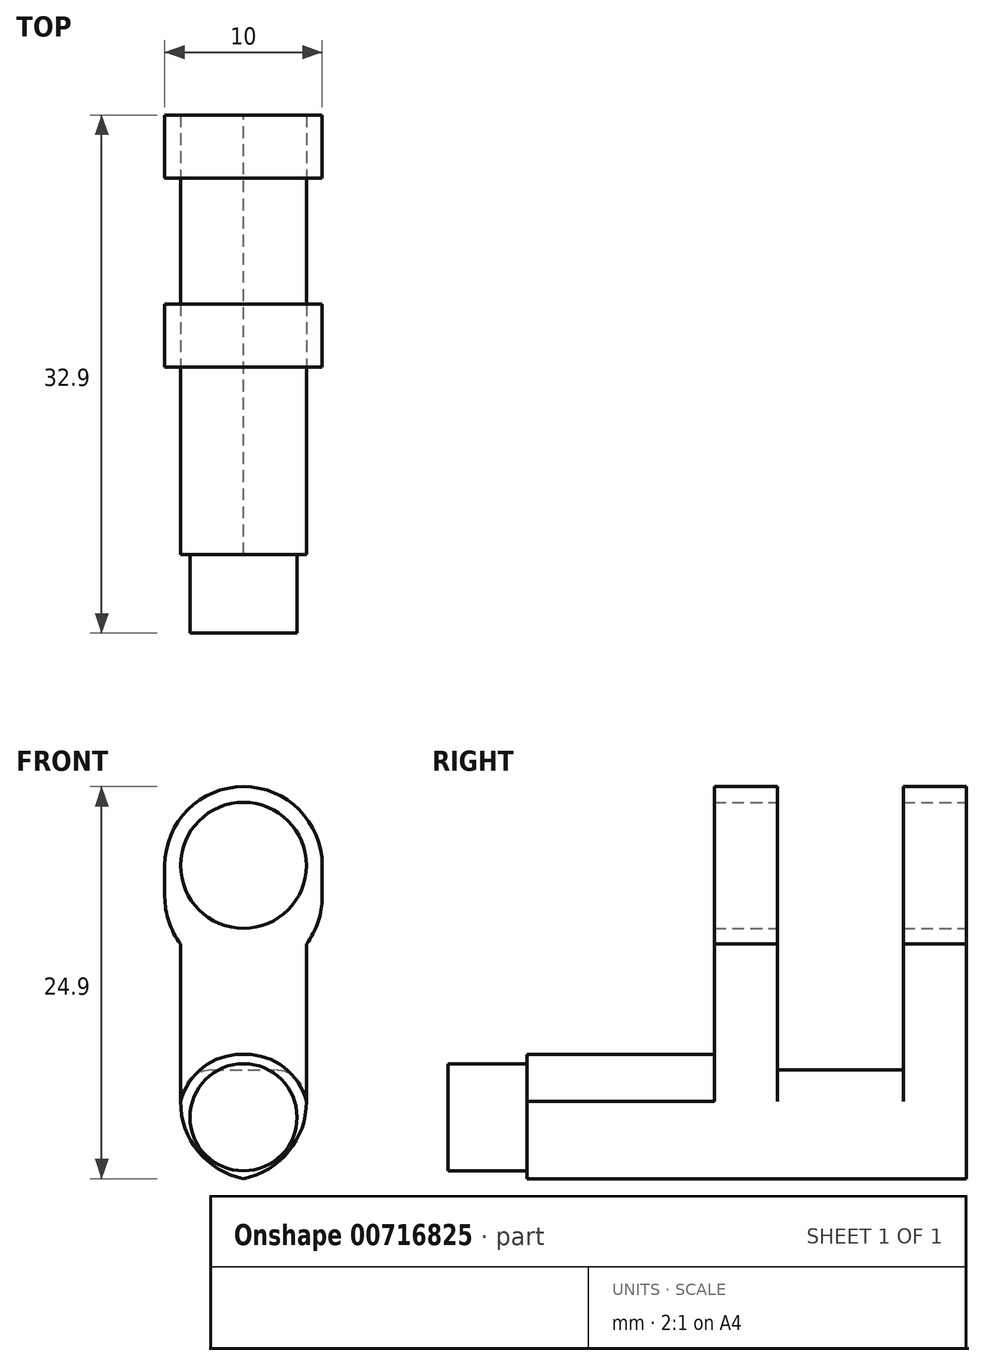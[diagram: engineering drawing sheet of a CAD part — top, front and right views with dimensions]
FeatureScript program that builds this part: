
annotation { "Feature Type Name" : "Feature", "Feature Type Description" : "" }
export const myFeature = defineFeature(function(context is Context, id is Id, definition is map)
    precondition{}
    {
        {
            var Q0;
            Q0=qCreatedBy(makeId("Front.planeOp"),FACE);
            var sketch = newSketch(context, id + "F0", { "sketchPlane" : qUnion([Q0])});
            skCircle(sketch, "E0", {"center": v(0, 0) * mm, "radius": 3.4 * mm});
            skSolve(sketch);
        }
        {
            var Q0;
            Q0=makeQuery(id+"F0.imprint","IMPRINT",FACE,{"disambiguationData":[TD([[makeQuery(id+"F0.imprint","IMPRINT",EDGE,{"derivedFrom":sQuery(id+"F0.wireOp",EDGE,"E0")}),1.0]])]});
            extrude(context, id + "F1", {"entities" : qUnion([Q0]), "depth" : 5 * mm, "offsetDistance" : 25 * mm});
        }
        {
            var Q0;
            Q0=makeQuery(id+"F1.opExtrude","CAP_FACE",FACE,{"disambiguationData":[OSD([sQuery(id+"F0.wireOp",EDGE,"E0")])],"isStart":true});
            var sketch = newSketch(context, id + "F2", { "sketchPlane" : qUnion([Q0])});
            skLineSegment(sketch, "E1.bottom", {"start": v(4, 4) * mm, "end": v(-4, 4) * mm});
            skLineSegment(sketch, "E1.top", {"start": v(4, -4) * mm, "end": v(-4, -4) * mm});
            skLineSegment(sketch, "E1.left", {"start": v(4, 4) * mm, "end": v(4, -4) * mm});
            skLineSegment(sketch, "E1.right", {"start": v(-4, 4) * mm, "end": v(-4, -4) * mm});
            skPoint(sketch, "E1.middle", {"position": v(0, 0) * mm});
            skSolve(sketch);
        }
        {
            var Q0;
            Q0 = qSketchRegion(id + "F2", true);
            extrude(context, id + "F3", {"entities" : qUnion([Q0]), "operationType" : NewBodyOperationType.ADD, "depth" : 14.9 * mm, "offsetDistance" : 25 * mm});
        }
        {
            var Q0;
            Q0=makeQuery(id+"F3.opExtrude","CAP_FACE",FACE,{"disambiguationData":[OSD([sQuery(id+"F2.wireOp",EDGE,"E1.bottom"),sQuery(id+"F2.wireOp",EDGE,"E1.top"),sQuery(id+"F2.wireOp",EDGE,"E1.left"),sQuery(id+"F2.wireOp",EDGE,"E1.right")])],"isStart":false});
            var sketch = newSketch(context, id + "F4", { "sketchPlane" : qUnion([Q0])});
            skLineSegment(sketch, "E2.bottom", {"start": v(-4, -4) * mm, "end": v(4, -4) * mm});
            skLineSegment(sketch, "E2.top", {"start": v(-4, 21) * mm, "end": v(4, 21) * mm});
            skLineSegment(sketch, "E2.left", {"start": v(-4, -4) * mm, "end": v(-4, 21) * mm});
            skLineSegment(sketch, "E2.right", {"start": v(4, -4) * mm, "end": v(4, 21) * mm});
            skSolve(sketch);
        }
        {
            var Q0;
            Q0 = qSketchRegion(id + "F4", true);
            extrude(context, id + "F5", {"entities" : qUnion([Q0]), "operationType" : NewBodyOperationType.ADD, "depth" : 10 * mm, "offsetDistance" : 25 * mm});
        }
        {
            var Q0;
            Q0=makeQuery(id+"F5.opExtrude","CAP_FACE",FACE,{"disambiguationData":[OSD([sQuery(id+"F4.wireOp",EDGE,"E2.bottom"),sQuery(id+"F4.wireOp",EDGE,"E2.top"),sQuery(id+"F4.wireOp",EDGE,"E2.left"),sQuery(id+"F4.wireOp",EDGE,"E2.right")])],"isStart":false});
            var sketch = newSketch(context, id + "F6", { "sketchPlane" : qUnion([Q0])});
            skLineSegment(sketch, "E3.bottom", {"start": v(-5, 21) * mm, "end": v(5, 21) * mm});
            skLineSegment(sketch, "E3.top", {"start": v(-5, 11) * mm, "end": v(5, 11) * mm});
            skLineSegment(sketch, "E3.left", {"start": v(-5, 21) * mm, "end": v(-5, 11) * mm});
            skLineSegment(sketch, "E3.right", {"start": v(5, 21) * mm, "end": v(5, 11) * mm});
            skSolve(sketch);
        }
        {
            var Q0;
            Q0 = qSketchRegion(id + "F6", true);
            extrude(context, id + "F7", {"entities" : qUnion([Q0]), "operationType" : NewBodyOperationType.ADD, "oppositeDirection" : true, "depth" : 10 * mm, "offsetDistance" : 25 * mm});
        }
        {
            var Q0;
            Q0=makeQuery(id+"F7.boolean.opBoolean","MERGE",FACE,{"derivedFrom":[makeQuery(id+"F5.opExtrude","CAP_FACE",FACE,{"disambiguationData":[OSD([sQuery(id+"F4.wireOp",EDGE,"E2.bottom"),sQuery(id+"F4.wireOp",EDGE,"E2.top"),sQuery(id+"F4.wireOp",EDGE,"E2.left"),sQuery(id+"F4.wireOp",EDGE,"E2.right")])],"isStart":false}),makeQuery(id+"F7.opExtrude","CAP_FACE",FACE,{"disambiguationData":[OSD([sQuery(id+"F6.wireOp",EDGE,"E3.bottom"),sQuery(id+"F6.wireOp",EDGE,"E3.top"),sQuery(id+"F6.wireOp",EDGE,"E3.left"),sQuery(id+"F6.wireOp",EDGE,"E3.right")])],"isStart":true})]});
            var sketch = newSketch(context, id + "F8", { "sketchPlane" : qUnion([Q0])});
            skCircle(sketch, "E4", {"center": v(0, 16) * mm, "radius": 4 * mm});
            skSolve(sketch);
        }
        {
            var Q0;
            Q0 = qSketchRegion(id + "F8", true);
            extrude(context, id + "F9", {"entities" : qUnion([Q0]), "operationType" : NewBodyOperationType.REMOVE, "endBound" : BoundingType.UP_TO_NEXT, "oppositeDirection" : true, "depth" : 25 * mm, "offsetDistance" : 25 * mm});
        }
        {
            var Q0;
            Q0=makeQuery(id+"F7.boolean.opBoolean","MERGE",FACE,{"derivedFrom":[makeQuery(id+"F5.opExtrude","SWEPT_FACE",FACE,{"disambiguationData":[OSD([sQuery(id+"F4.wireOp",EDGE,"E2.top")])]}),makeQuery(id+"F7.opExtrude","SWEPT_FACE",FACE,{"disambiguationData":[OSD([sQuery(id+"F6.wireOp",EDGE,"E3.bottom")])]})]});
            var sketch = newSketch(context, id + "F10", { "sketchPlane" : qUnion([Q0])});
            skLineSegment(sketch, "E5.bottom", {"start": v(-5, 23.9) * mm, "end": v(5, 23.9) * mm});
            skLineSegment(sketch, "E5.top", {"start": v(-5, 15.9) * mm, "end": v(5, 15.9) * mm});
            skLineSegment(sketch, "E5.left", {"start": v(-5, 23.9) * mm, "end": v(-5, 15.9) * mm});
            skLineSegment(sketch, "E5.right", {"start": v(5, 23.9) * mm, "end": v(5, 15.9) * mm});
            skSolve(sketch);
        }
        {
            var Q0;
            Q0 = qSketchRegion(id + "F10", true);
            extrude(context, id + "F11", {"entities" : qUnion([Q0]), "operationType" : NewBodyOperationType.REMOVE, "oppositeDirection" : true, "depth" : 18 * mm, "offsetDistance" : 25 * mm});
        }
        {
            var Q0;
            {var subQ0=sQuery(id+"F6.wireOp",EDGE,"E3.left");var subQ1=sQuery(id+"F6.wireOp",EDGE,"E3.top");Q0=makeQuery(id+"F11.boolean.opBoolean","SPLIT",EDGE,{"disambiguationData":[TD([makeQuery(id+"F11.opExtrude","SWEPT_FACE",FACE,{"disambiguationData":[OSD([sQuery(id+"F10.wireOp",EDGE,"E5.top")])]})])],"derivedFrom":makeQuery(id+"F7.opExtrude","SWEPT_EDGE",EDGE,{"disambiguationData":[OSD([subQ1,subQ0])]})});}
            var Q1;
            {var subQ0=sQuery(id+"F6.wireOp",EDGE,"E3.left");var subQ1=sQuery(id+"F6.wireOp",EDGE,"E3.top");Q1=makeQuery(id+"F11.boolean.opBoolean","SPLIT",EDGE,{"disambiguationData":[TD([makeQuery(id+"F11.opExtrude","SWEPT_FACE",FACE,{"disambiguationData":[OSD([sQuery(id+"F10.wireOp",EDGE,"E5.bottom")])]})])],"derivedFrom":makeQuery(id+"F7.opExtrude","SWEPT_EDGE",EDGE,{"disambiguationData":[OSD([subQ1,subQ0])]})});}
            var Q2;
            {var subQ0=sQuery(id+"F6.wireOp",EDGE,"E3.right");var subQ1=sQuery(id+"F6.wireOp",EDGE,"E3.top");Q2=makeQuery(id+"F11.boolean.opBoolean","SPLIT",EDGE,{"disambiguationData":[TD([makeQuery(id+"F11.opExtrude","SWEPT_FACE",FACE,{"disambiguationData":[OSD([sQuery(id+"F10.wireOp",EDGE,"E5.top")])]})])],"derivedFrom":makeQuery(id+"F7.opExtrude","SWEPT_EDGE",EDGE,{"disambiguationData":[OSD([subQ1,subQ0])]})});}
            var Q3;
            {var subQ0=sQuery(id+"F6.wireOp",EDGE,"E3.right");var subQ1=sQuery(id+"F6.wireOp",EDGE,"E3.top");Q3=makeQuery(id+"F11.boolean.opBoolean","SPLIT",EDGE,{"disambiguationData":[TD([makeQuery(id+"F11.opExtrude","SWEPT_FACE",FACE,{"disambiguationData":[OSD([sQuery(id+"F10.wireOp",EDGE,"E5.bottom")])]})])],"derivedFrom":makeQuery(id+"F7.opExtrude","SWEPT_EDGE",EDGE,{"disambiguationData":[OSD([subQ1,subQ0])]})});}
            var Q4;
            {var subQ0=sQuery(id+"F6.wireOp",EDGE,"E3.right");var subQ1=sQuery(id+"F6.wireOp",EDGE,"E3.bottom");Q4=makeQuery(id+"F11.boolean.opBoolean","SPLIT",EDGE,{"disambiguationData":[TD([makeQuery(id+"F11.opExtrude","SWEPT_FACE",FACE,{"disambiguationData":[OSD([sQuery(id+"F10.wireOp",EDGE,"E5.bottom")])]})])],"derivedFrom":makeQuery(id+"F7.opExtrude","SWEPT_EDGE",EDGE,{"disambiguationData":[OSD([subQ1,subQ0])]})});}
            var Q5;
            {var subQ0=sQuery(id+"F6.wireOp",EDGE,"E3.left");var subQ1=sQuery(id+"F6.wireOp",EDGE,"E3.bottom");Q5=makeQuery(id+"F11.boolean.opBoolean","SPLIT",EDGE,{"disambiguationData":[TD([makeQuery(id+"F11.opExtrude","SWEPT_FACE",FACE,{"disambiguationData":[OSD([sQuery(id+"F10.wireOp",EDGE,"E5.bottom")])]})])],"derivedFrom":makeQuery(id+"F7.opExtrude","SWEPT_EDGE",EDGE,{"disambiguationData":[OSD([subQ1,subQ0])]})});}
            var Q6;
            {var subQ0=sQuery(id+"F6.wireOp",EDGE,"E3.bottom");var subQ2=sQuery(id+"F6.wireOp",EDGE,"E3.right");Q6=makeQuery(id+"F11.boolean.opBoolean","SPLIT",EDGE,{"disambiguationData":[TD([makeQuery(id+"F11.opExtrude","SWEPT_FACE",FACE,{"disambiguationData":[OSD([sQuery(id+"F10.wireOp",EDGE,"E5.top")])]})])],"derivedFrom":makeQuery(id+"F7.opExtrude","SWEPT_EDGE",EDGE,{"disambiguationData":[OSD([subQ0,subQ2])]})});}
            var Q7;
            {var subQ0=sQuery(id+"F6.wireOp",EDGE,"E3.bottom");var subQ2=sQuery(id+"F6.wireOp",EDGE,"E3.left");Q7=makeQuery(id+"F11.boolean.opBoolean","SPLIT",EDGE,{"disambiguationData":[TD([makeQuery(id+"F11.opExtrude","SWEPT_FACE",FACE,{"disambiguationData":[OSD([sQuery(id+"F10.wireOp",EDGE,"E5.top")])]})])],"derivedFrom":makeQuery(id+"F7.opExtrude","SWEPT_EDGE",EDGE,{"disambiguationData":[OSD([subQ0,subQ2])]})});}
            fillet(context, id + "F12", {"entities" : qUnion([Q0, Q1, Q2, Q3, Q4, Q5, Q6, Q7]), "radius" : 5 * mm, "tangentPropagation" : true, "allowEdgeOverflow" : false});
        }
        {
            var Q0;
            Q0=makeQuery(id+"F7.boolean.opBoolean","MERGE",FACE,{"derivedFrom":[makeQuery(id+"F5.opExtrude","CAP_FACE",FACE,{"disambiguationData":[OSD([sQuery(id+"F4.wireOp",EDGE,"E2.bottom"),sQuery(id+"F4.wireOp",EDGE,"E2.top"),sQuery(id+"F4.wireOp",EDGE,"E2.left"),sQuery(id+"F4.wireOp",EDGE,"E2.right")])],"isStart":false}),makeQuery(id+"F7.opExtrude","CAP_FACE",FACE,{"disambiguationData":[OSD([sQuery(id+"F6.wireOp",EDGE,"E3.bottom"),sQuery(id+"F6.wireOp",EDGE,"E3.top"),sQuery(id+"F6.wireOp",EDGE,"E3.left"),sQuery(id+"F6.wireOp",EDGE,"E3.right")])],"isStart":true})]});
            var sketch = newSketch(context, id + "F13", { "sketchPlane" : qUnion([Q0])});
            skArc(sketch, "E6.0.0", {"start": v(5, 16) * mm, "mid": v(0, 21) * mm, "end": v(-5, 16) * mm});
            skLineSegment(sketch, "E6.0.1", {"start": v(-5, 16) * mm, "end": v(-5, 14) * mm});
            skArc(sketch, "E6.0.2", {"start": v(-5, 14) * mm, "mid": v(-4.74, 12.42) * mm, "end": v(-4, 11) * mm});
            skLineSegment(sketch, "E6.0.3", {"start": v(-4, 11) * mm, "end": v(-4, -4) * mm});
            skLineSegment(sketch, "E6.0.4", {"start": v(-4, -4) * mm, "end": v(4, -4) * mm});
            skLineSegment(sketch, "E6.0.5", {"start": v(4, -4) * mm, "end": v(4, 11) * mm});
            skArc(sketch, "E6.0.6", {"start": v(4, 11) * mm, "mid": v(4.74, 12.42) * mm, "end": v(5, 14) * mm});
            skLineSegment(sketch, "E6.0.7", {"start": v(5, 14) * mm, "end": v(5, 16) * mm});
            skCircle(sketch, "E7.0", {"center": v(0, 16) * mm, "radius": 4 * mm});
            skSolve(sketch);
        }
        {
            var Q0;
            Q0 = qSketchRegion(id + "F13", true);
            extrude(context, id + "F14", {"entities" : qUnion([Q0]), "operationType" : NewBodyOperationType.ADD, "depth" : 3 * mm, "offsetDistance" : 25 * mm});
        }
        {
            var Q0;
            Q0=makeQuery(id+"F7.boolean.opBoolean","MERGE",FACE,{"derivedFrom":[makeQuery(id+"F5.opExtrude","CAP_FACE",FACE,{"disambiguationData":[OSD([sQuery(id+"F4.wireOp",EDGE,"E2.bottom"),sQuery(id+"F4.wireOp",EDGE,"E2.top"),sQuery(id+"F4.wireOp",EDGE,"E2.left"),sQuery(id+"F4.wireOp",EDGE,"E2.right")])],"isStart":true}),makeQuery(id+"F7.opExtrude","CAP_FACE",FACE,{"disambiguationData":[OSD([sQuery(id+"F6.wireOp",EDGE,"E3.bottom"),sQuery(id+"F6.wireOp",EDGE,"E3.top"),sQuery(id+"F6.wireOp",EDGE,"E3.left"),sQuery(id+"F6.wireOp",EDGE,"E3.right")])],"isStart":false})]});
            var sketch = newSketch(context, id + "F15", { "sketchPlane" : qUnion([Q0])});
            skLineSegment(sketch, "E8.0.0", {"start": v(4, 4) * mm, "end": v(4, 11) * mm});
            skArc(sketch, "E8.0.1", {"start": v(4, 11) * mm, "mid": v(4.74, 12.42) * mm, "end": v(5, 14) * mm});
            skLineSegment(sketch, "E8.0.2", {"start": v(5, 14) * mm, "end": v(5, 16) * mm});
            skArc(sketch, "E8.0.3", {"start": v(5, 16) * mm, "mid": v(0, 21) * mm, "end": v(-5, 16) * mm});
            skLineSegment(sketch, "E8.0.4", {"start": v(-5, 16) * mm, "end": v(-5, 14) * mm});
            skArc(sketch, "E8.0.5", {"start": v(-5, 14) * mm, "mid": v(-4.74, 12.42) * mm, "end": v(-4, 11) * mm});
            skLineSegment(sketch, "E8.0.6", {"start": v(-4, 11) * mm, "end": v(-4, 4) * mm});
            skLineSegment(sketch, "E8.0.7", {"start": v(-4, 4) * mm, "end": v(4, 4) * mm});
            skCircle(sketch, "E9.0", {"center": v(0, 16) * mm, "radius": 4 * mm});
            skSolve(sketch);
        }
        {
            var Q0;
            Q0 = qSketchRegion(id + "F15", true);
            extrude(context, id + "F16", {"entities" : qUnion([Q0]), "operationType" : NewBodyOperationType.ADD, "depth" : 3 * mm, "offsetDistance" : 25 * mm});
        }
        {
            var Q0;
            Q0=makeQuery(id+"F14.boolean.opBoolean","MERGE",EDGE,{"derivedFrom":[makeQuery(id+"F5.boolean.opBoolean","MERGE",EDGE,{"derivedFrom":[makeQuery(id+"F3.opExtrude","SWEPT_EDGE",EDGE,{"disambiguationData":[OSD([sQuery(id+"F2.wireOp",EDGE,"E1.top"),sQuery(id+"F2.wireOp",EDGE,"E1.right")])]}),makeQuery(id+"F5.opExtrude","SWEPT_EDGE",EDGE,{"disambiguationData":[OSD([sQuery(id+"F4.wireOp",EDGE,"E2.bottom"),sQuery(id+"F4.wireOp",EDGE,"E2.left")])]})]}),makeQuery(id+"F14.opExtrude","SWEPT_EDGE",EDGE,{"disambiguationData":[OSD([sQuery(id+"F13.wireOp",EDGE,"E6.0.3"),sQuery(id+"F13.wireOp",EDGE,"E6.0.4")])]})]});
            var Q1;
            Q1=makeQuery(id+"F14.boolean.opBoolean","MERGE",EDGE,{"derivedFrom":[makeQuery(id+"F5.boolean.opBoolean","MERGE",EDGE,{"derivedFrom":[makeQuery(id+"F3.opExtrude","SWEPT_EDGE",EDGE,{"disambiguationData":[OSD([sQuery(id+"F2.wireOp",EDGE,"E1.top"),sQuery(id+"F2.wireOp",EDGE,"E1.left")])]}),makeQuery(id+"F5.opExtrude","SWEPT_EDGE",EDGE,{"disambiguationData":[OSD([sQuery(id+"F4.wireOp",EDGE,"E2.bottom"),sQuery(id+"F4.wireOp",EDGE,"E2.right")])]})]}),makeQuery(id+"F14.opExtrude","SWEPT_EDGE",EDGE,{"disambiguationData":[OSD([sQuery(id+"F13.wireOp",EDGE,"E6.0.4"),sQuery(id+"F13.wireOp",EDGE,"E6.0.5")])]})]});
            fillet(context, id + "F17", {"entities" : qUnion([Q0, Q1]), "radius" : 5 * mm, "tangentPropagation" : true, "allowEdgeOverflow" : false});
        }
        {
            var Q0;
            Q0=makeQuery(id+"F3.opExtrude","SWEPT_EDGE",EDGE,{"disambiguationData":[OSD([sQuery(id+"F2.wireOp",EDGE,"E1.bottom"),sQuery(id+"F2.wireOp",EDGE,"E1.right")])]});
            var Q1;
            Q1=makeQuery(id+"F3.opExtrude","SWEPT_EDGE",EDGE,{"disambiguationData":[OSD([sQuery(id+"F2.wireOp",EDGE,"E1.bottom"),sQuery(id+"F2.wireOp",EDGE,"E1.left")])]});
            fillet(context, id + "F18", {"entities" : qUnion([Q0, Q1]), "radius" : 4 * mm, "tangentPropagation" : true, "allowEdgeOverflow" : false});
        }
        {
            var Q0;
            Q0=makeQuery(id+"F11.boolean.opBoolean","INTERSECT",EDGE,{"derivedFrom":[makeQuery(id+"F5.boolean.opBoolean","MERGE",FACE,{"derivedFrom":[makeQuery(id+"F3.opExtrude","SWEPT_FACE",FACE,{"disambiguationData":[OSD([sQuery(id+"F2.wireOp",EDGE,"E1.right")])]}),makeQuery(id+"F5.opExtrude","SWEPT_FACE",FACE,{"disambiguationData":[OSD([sQuery(id+"F4.wireOp",EDGE,"E2.left")])]})]}),makeQuery(id+"F11.opExtrude","CAP_FACE",FACE,{"disambiguationData":[OSD([sQuery(id+"F10.wireOp",EDGE,"E5.bottom"),sQuery(id+"F10.wireOp",EDGE,"E5.top"),sQuery(id+"F10.wireOp",EDGE,"E5.left"),sQuery(id+"F10.wireOp",EDGE,"E5.right")])],"isStart":false})]});
            var Q1;
            Q1=makeQuery(id+"F11.boolean.opBoolean","INTERSECT",EDGE,{"derivedFrom":[makeQuery(id+"F5.boolean.opBoolean","MERGE",FACE,{"derivedFrom":[makeQuery(id+"F3.opExtrude","SWEPT_FACE",FACE,{"disambiguationData":[OSD([sQuery(id+"F2.wireOp",EDGE,"E1.left")])]}),makeQuery(id+"F5.opExtrude","SWEPT_FACE",FACE,{"disambiguationData":[OSD([sQuery(id+"F4.wireOp",EDGE,"E2.right")])]})]}),makeQuery(id+"F11.opExtrude","CAP_FACE",FACE,{"disambiguationData":[OSD([sQuery(id+"F10.wireOp",EDGE,"E5.bottom"),sQuery(id+"F10.wireOp",EDGE,"E5.top"),sQuery(id+"F10.wireOp",EDGE,"E5.left"),sQuery(id+"F10.wireOp",EDGE,"E5.right")])],"isStart":false})]});
            fillet(context, id + "F19", {"entities" : qUnion([Q0, Q1]), "radius" : 2 * mm, "tangentPropagation" : true, "allowEdgeOverflow" : false});
        }
    });
